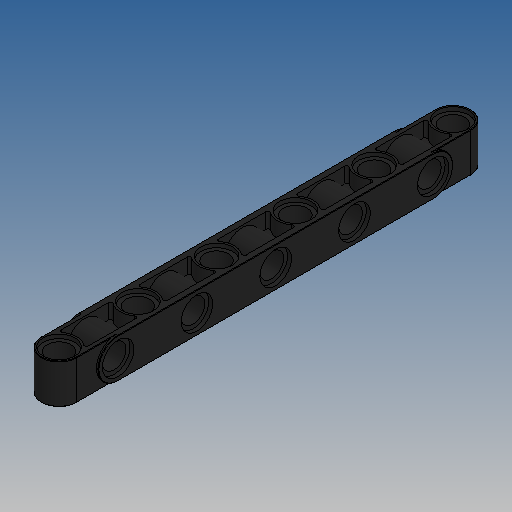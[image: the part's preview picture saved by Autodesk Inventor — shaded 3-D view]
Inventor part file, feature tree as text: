
AUTODESK INVENTOR PART (.ipt)
format: ipt  version: 2025 (Build 290162010, 162A)  size: 468,992 bytes
history: native  units: mm
features: sketch x8, extrude x7, mirror x3, fillet x2, delete_face x1, hole x1, pattern_linear x1
ambient origin geometry x8: Origin, YZ Plane, XZ Plane, XY Plane, X Axis, Y Axis, Z Axis, Center Point
bodies: Solid1 (feature_tree)
feature tree (23):
  extrude  "Extrusion1"  Depth=7.2mm
  sketch  "Sketch6"  dims[d48=80.0mm d49=6.4mm d50=4.8mm]
  extrude  "Extrusion7"  Depth=0.8mm TaperAngle=0.0deg
  extrude  "Extrusion8"  Depth=6.4mm
  mirror  "Mirror1"
  fillet  "Fillet2"  Radius=4.8mm
  mirror  "Spiegeln2"
  extrude  "Extrusion9"  Depth=0.8mm
  delete_face  "Fläche löschen1"
  fillet  "Rundung3"  Radius=50.0mm
  mirror  "Spiegeln3"
  extrude  "Extrusion10"  Depth=0.1mm
  extrude  "Extrusion11"  Depth=0.1mm
  extrude  "Extrusion12"  Depth=7.2mm TaperAngle=0.0deg
  hole  "Bohrung1"  [1 undecoded]
  pattern_linear  "Rechteckige Anordnung1"  Spacing1=0.0mm  [1 undecoded]
  sketch  "Sketch1"  dims[d14=8.0mm d15=0.0mm d32=7.2mm]
  sketch  "Skizze - Rechteckige Anordnung1"  dims[d41=0.8mm d42=0.0mm d43=3.1mm d44=0.0mm]
  sketch  "Skizze9"  dims[d51=16.0mm d52=0.8mm d53=50.0mm]
  sketch  "Skizze10"  dims[d55=16.0mm d56=10.0mm d58=10.0mm d60=0.4mm d61=0.1mm]
  sketch  "Skizze11"  dims[d63=0.4mm d64=0.0mm d65=0.1mm]
  sketch  "Skizze12"  dims[d66=7.2mm d67=0.4mm d68=0.0mm]
  sketch  "Skizze13"  dims[d69=6.4mm d70=0.8mm d71=0.0mm d72=0.8mm d73=0.0mm d74=4.8mm d75=40.0mm d76=4.0mm d77=2.0mm d78=90.0deg d79=8.0mm d80=20.594885mm d81=50.0mm d83=16.0mm d62=0.5mm]
note: 2 required parameter values undecoded (feature->parameter linkage not recoverable at this tier; creation-order binding heuristic only, values carry confidence <= 0.55)
